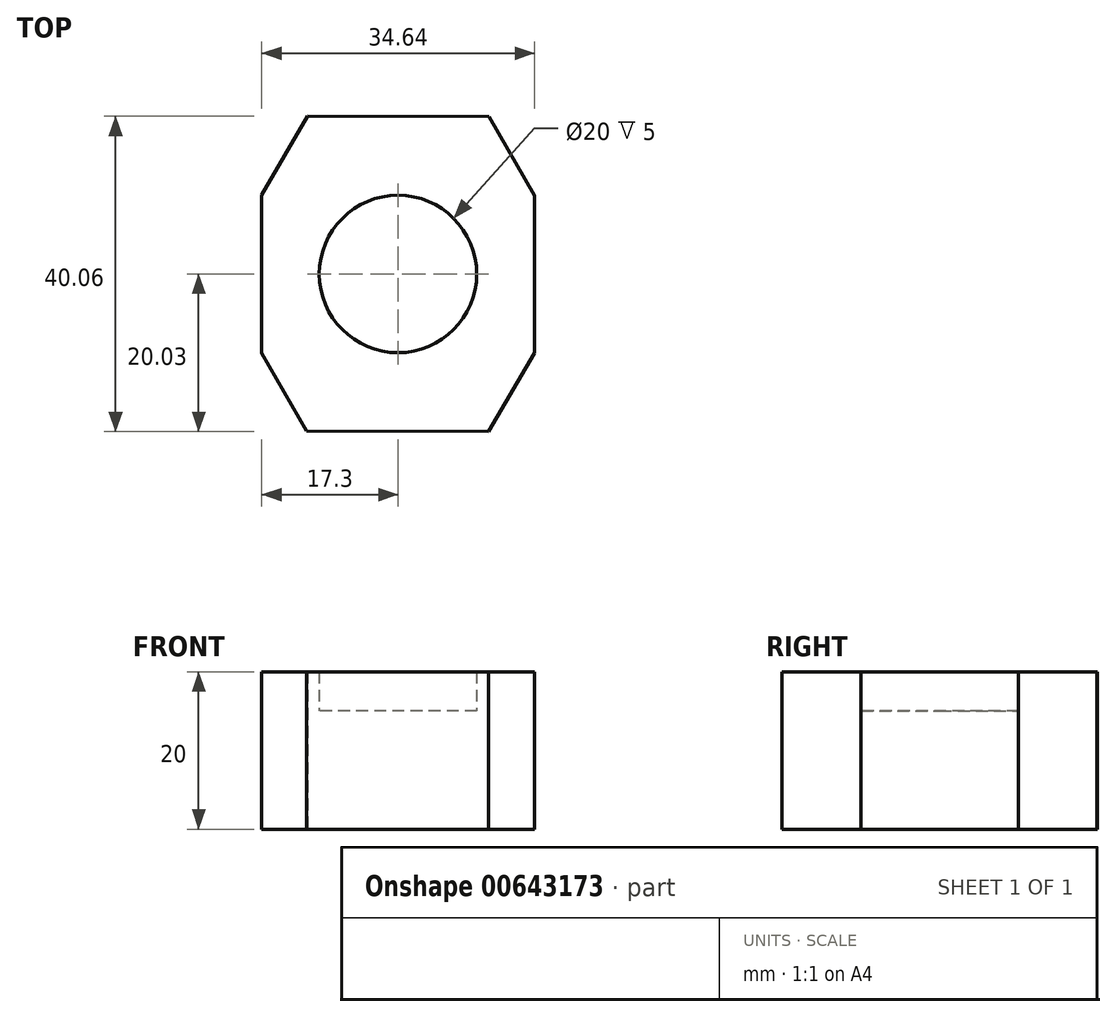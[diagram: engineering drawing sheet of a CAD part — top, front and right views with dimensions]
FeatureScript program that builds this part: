
annotation { "Feature Type Name" : "Feature", "Feature Type Description" : "" }
export const myFeature = defineFeature(function(context is Context, id is Id, definition is map)
    precondition{}
    {
        {
            var Q0;
            Q0=qCreatedBy(makeId("Top.planeOp"),FACE);
            var sketch = newSketch(context, id + "F0", { "sketchPlane" : qUnion([Q0])});
            skLineSegment(sketch, "E0.2", {"start": v(11.49, -20.03) * mm, "end": v(-11.6, -19.97) * mm});
            skLineSegment(sketch, "E0.5", {"start": v(-11.5, 20.03) * mm, "end": v(11.59, 19.97) * mm});
            skPoint(sketch, "E0.0.midPoint", {"position": v(17.34, 9.96) * mm});
            skPoint(sketch, "E1", {"position": v(-17.3, 10.04) * mm});
            skPoint(sketch, "E2", {"position": v(-17.3, -10.04) * mm});
            skLineSegment(sketch, "E3", {"start": v(-17.3, 10.04) * mm, "end": v(-17.3, -10.04) * mm});
            skLineSegment(sketch, "E4", {"start": v(17.34, 9.96) * mm, "end": v(17.34, -10.04) * mm});
            skLineSegment(sketch, "E5", {"start": v(-11.5, 20.03) * mm, "end": v(-17.3, 10.04) * mm});
            skLineSegment(sketch, "E6", {"start": v(-17.3, -10.04) * mm, "end": v(-11.6, -19.97) * mm});
            skLineSegment(sketch, "E7", {"start": v(11.49, -20.03) * mm, "end": v(17.34, -10.04) * mm});
            skLineSegment(sketch, "E8", {"start": v(17.34, 9.96) * mm, "end": v(11.59, 19.97) * mm});
            skLineSegment(sketch, "E9", {"start": v(0.04, 20) * mm, "end": v(0.04, -20) * mm});
            skSolve(sketch);
        }
        {
            var Q0;
            Q0=makeQuery(id+"F0.imprint","IMPRINT",FACE,{"disambiguationData":[TD([[makeQuery(id+"F0.imprint","IMPRINT",EDGE,{"derivedFrom":sQuery(id+"F0.wireOp",EDGE,"E0.2")}),-1.0]])]});
            extrude(context, id + "F1", {"entities" : qUnion([Q0]), "depth" : 15 * mm, "offsetDistance" : 25 * mm});
        }
        {
            var Q0;
            Q0=makeQuery(id+"F1.opExtrude","CAP_FACE",FACE,{"disambiguationData":[OSD([sQuery(id+"F0.wireOp",EDGE,"E0.2"),sQuery(id+"F0.wireOp",EDGE,"E0.5"),sQuery(id+"F0.wireOp",EDGE,"E3"),sQuery(id+"F0.wireOp",EDGE,"E4"),sQuery(id+"F0.wireOp",EDGE,"E5"),sQuery(id+"F0.wireOp",EDGE,"E6"),sQuery(id+"F0.wireOp",EDGE,"E7"),sQuery(id+"F0.wireOp",EDGE,"E8")])],"isStart":false});
            var sketch = newSketch(context, id + "F2", { "sketchPlane" : qUnion([Q0])});
            skCircle(sketch, "E10", {"center": v(0, 0) * mm, "radius": 10 * mm});
            skLineSegment(sketch, "E11", {"start": v(0, 0) * mm, "end": v(10, 0) * mm});
            skSolve(sketch);
        }
        {
            var Q0;
            Q0=makeQuery(id+"F2.imprint","IMPRINT",FACE,{"disambiguationData":[TD([[makeQuery(id+"F2.imprint","IMPRINT",EDGE,{"derivedFrom":sQuery(id+"F2.wireOp",EDGE,"E10")}),-1.0]])]});
            extrude(context, id + "F3", {"entities" : qUnion([Q0]), "operationType" : NewBodyOperationType.ADD, "depth" : 5 * mm, "offsetDistance" : 25 * mm});
        }
    });
